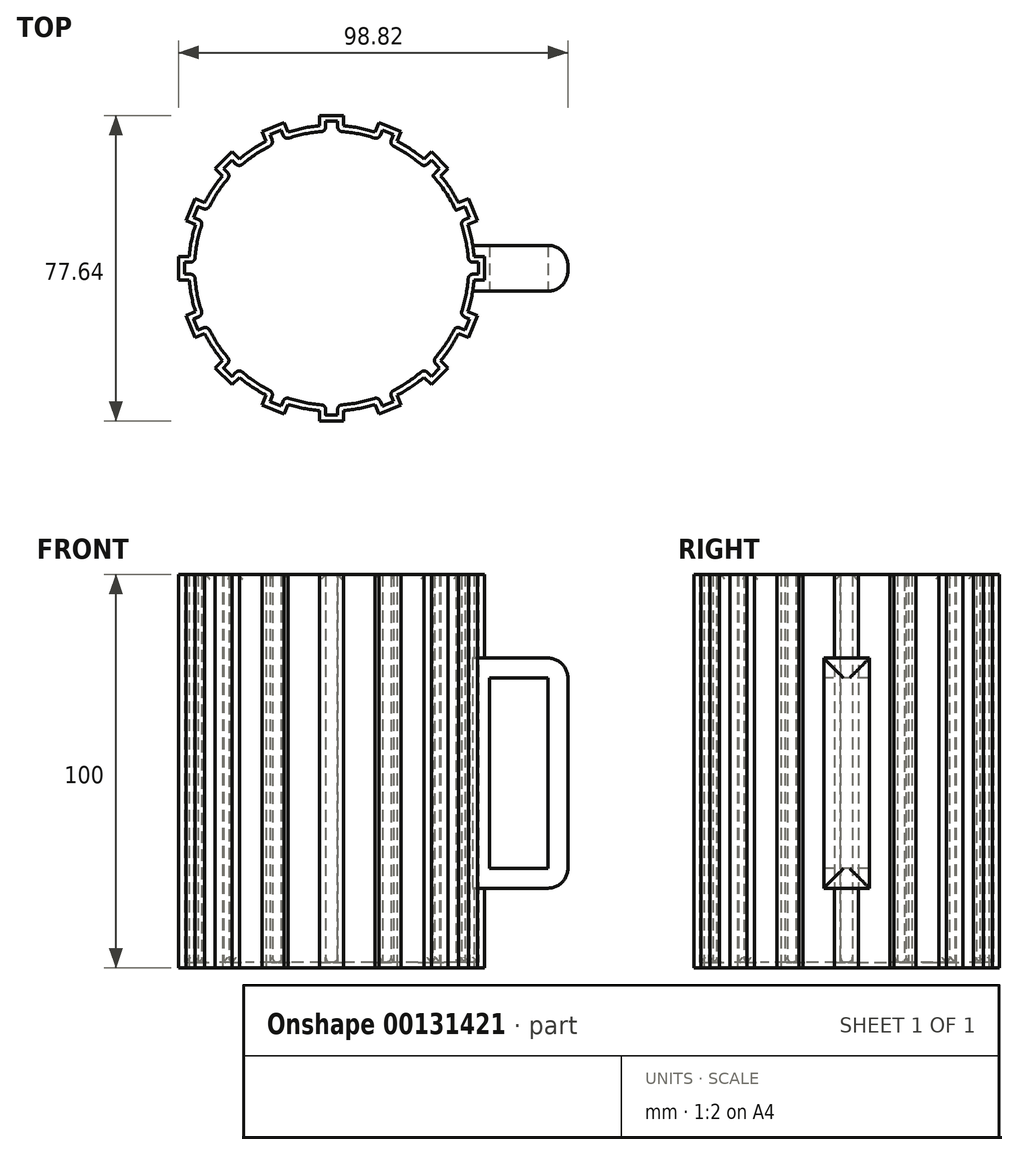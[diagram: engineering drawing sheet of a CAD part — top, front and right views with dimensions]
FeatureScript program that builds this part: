
annotation { "Feature Type Name" : "Feature", "Feature Type Description" : "" }
export const myFeature = defineFeature(function(context is Context, id is Id, definition is map)
    precondition{}
    {
        {
            var Q0;
            Q0=qCreatedBy(makeId("Top.planeOp"),FACE);
            var sketch = newSketch(context, id + "F0", { "sketchPlane" : qUnion([Q0])});
            skCircle(sketch, "E0", {"center": v(0, 0) * mm, "radius": 36.3 * mm});
            skLineSegment(sketch, "E1.bottom", {"start": v(3.02, 38.82) * mm, "end": v(-3.02, 38.82) * mm});
            skLineSegment(sketch, "E1.top", {"start": v(3.02, 33.79) * mm, "end": v(-3.02, 33.79) * mm});
            skLineSegment(sketch, "E1.left", {"start": v(3.02, 38.82) * mm, "end": v(3.02, 33.79) * mm});
            skLineSegment(sketch, "E1.right", {"start": v(-3.02, 38.82) * mm, "end": v(-3.02, 33.79) * mm});
            skPoint(sketch, "E1.middle", {"position": v(0, 36.3) * mm});
            skLineSegment(sketch, "E2.1.0", {"start": v(12.07, 37.02) * mm, "end": v(10.14, 32.37) * mm});
            skLineSegment(sketch, "E2.1.1", {"start": v(17.65, 34.7) * mm, "end": v(12.07, 37.02) * mm});
            skLineSegment(sketch, "E2.1.2", {"start": v(17.65, 34.7) * mm, "end": v(15.72, 30.06) * mm});
            skLineSegment(sketch, "E2.2.0", {"start": v(25.32, 29.59) * mm, "end": v(21.76, 26.03) * mm});
            skLineSegment(sketch, "E2.2.1", {"start": v(29.59, 25.32) * mm, "end": v(25.32, 29.59) * mm});
            skLineSegment(sketch, "E2.2.2", {"start": v(29.59, 25.32) * mm, "end": v(26.03, 21.76) * mm});
            skLineSegment(sketch, "E2.3.0", {"start": v(34.7, 17.65) * mm, "end": v(30.06, 15.72) * mm});
            skLineSegment(sketch, "E2.3.1", {"start": v(37.02, 12.07) * mm, "end": v(34.7, 17.65) * mm});
            skLineSegment(sketch, "E2.3.2", {"start": v(37.02, 12.07) * mm, "end": v(32.37, 10.14) * mm});
            skLineSegment(sketch, "E2.4.0", {"start": v(38.82, 3.02) * mm, "end": v(33.79, 3.02) * mm});
            skLineSegment(sketch, "E2.4.1", {"start": v(38.82, -3.02) * mm, "end": v(38.82, 3.02) * mm});
            skLineSegment(sketch, "E2.4.2", {"start": v(38.82, -3.02) * mm, "end": v(33.79, -3.02) * mm});
            skLineSegment(sketch, "E2.5.0", {"start": v(37.02, -12.07) * mm, "end": v(32.37, -10.14) * mm});
            skLineSegment(sketch, "E2.5.1", {"start": v(34.7, -17.65) * mm, "end": v(37.02, -12.07) * mm});
            skLineSegment(sketch, "E2.5.2", {"start": v(34.7, -17.65) * mm, "end": v(30.06, -15.72) * mm});
            skLineSegment(sketch, "E2.6.0", {"start": v(29.59, -25.32) * mm, "end": v(26.03, -21.76) * mm});
            skLineSegment(sketch, "E2.6.1", {"start": v(25.32, -29.59) * mm, "end": v(29.59, -25.32) * mm});
            skLineSegment(sketch, "E2.6.2", {"start": v(25.32, -29.59) * mm, "end": v(21.76, -26.03) * mm});
            skLineSegment(sketch, "E2.7.0", {"start": v(17.65, -34.7) * mm, "end": v(15.72, -30.06) * mm});
            skLineSegment(sketch, "E2.7.1", {"start": v(12.07, -37.02) * mm, "end": v(17.65, -34.7) * mm});
            skLineSegment(sketch, "E2.7.2", {"start": v(12.07, -37.02) * mm, "end": v(10.14, -32.37) * mm});
            skLineSegment(sketch, "E2.8.0", {"start": v(3.02, -38.82) * mm, "end": v(3.02, -33.79) * mm});
            skLineSegment(sketch, "E2.8.1", {"start": v(-3.02, -38.82) * mm, "end": v(3.02, -38.82) * mm});
            skLineSegment(sketch, "E2.8.2", {"start": v(-3.02, -38.82) * mm, "end": v(-3.02, -33.79) * mm});
            skLineSegment(sketch, "E2.9.0", {"start": v(-12.07, -37.02) * mm, "end": v(-10.14, -32.37) * mm});
            skLineSegment(sketch, "E2.9.1", {"start": v(-17.65, -34.7) * mm, "end": v(-12.07, -37.02) * mm});
            skLineSegment(sketch, "E2.9.2", {"start": v(-17.65, -34.7) * mm, "end": v(-15.72, -30.06) * mm});
            skLineSegment(sketch, "E2.10.0", {"start": v(-25.32, -29.59) * mm, "end": v(-21.76, -26.03) * mm});
            skLineSegment(sketch, "E2.10.1", {"start": v(-29.59, -25.32) * mm, "end": v(-25.32, -29.59) * mm});
            skLineSegment(sketch, "E2.10.2", {"start": v(-29.59, -25.32) * mm, "end": v(-26.03, -21.76) * mm});
            skLineSegment(sketch, "E2.11.0", {"start": v(-34.7, -17.65) * mm, "end": v(-30.06, -15.72) * mm});
            skLineSegment(sketch, "E2.11.1", {"start": v(-37.02, -12.07) * mm, "end": v(-34.7, -17.65) * mm});
            skLineSegment(sketch, "E2.11.2", {"start": v(-37.02, -12.07) * mm, "end": v(-32.37, -10.14) * mm});
            skLineSegment(sketch, "E2.12.0", {"start": v(-38.82, -3.02) * mm, "end": v(-33.79, -3.02) * mm});
            skLineSegment(sketch, "E2.12.1", {"start": v(-38.82, 3.02) * mm, "end": v(-38.82, -3.02) * mm});
            skLineSegment(sketch, "E2.12.2", {"start": v(-38.82, 3.02) * mm, "end": v(-33.79, 3.02) * mm});
            skLineSegment(sketch, "E2.13.0", {"start": v(-37.02, 12.07) * mm, "end": v(-32.37, 10.14) * mm});
            skLineSegment(sketch, "E2.13.1", {"start": v(-34.7, 17.65) * mm, "end": v(-37.02, 12.07) * mm});
            skLineSegment(sketch, "E2.13.2", {"start": v(-34.7, 17.65) * mm, "end": v(-30.06, 15.72) * mm});
            skLineSegment(sketch, "E2.14.0", {"start": v(-29.59, 25.32) * mm, "end": v(-26.03, 21.76) * mm});
            skLineSegment(sketch, "E2.14.1", {"start": v(-25.32, 29.59) * mm, "end": v(-29.59, 25.32) * mm});
            skLineSegment(sketch, "E2.14.2", {"start": v(-25.32, 29.59) * mm, "end": v(-21.76, 26.03) * mm});
            skLineSegment(sketch, "E2.15.0", {"start": v(-17.65, 34.7) * mm, "end": v(-15.72, 30.06) * mm});
            skLineSegment(sketch, "E2.15.1", {"start": v(-12.07, 37.02) * mm, "end": v(-17.65, 34.7) * mm});
            skLineSegment(sketch, "E2.15.2", {"start": v(-12.07, 37.02) * mm, "end": v(-10.14, 32.37) * mm});
            skLineSegment(sketch, "E2.anchor1", {"start": v(0, 0) * mm, "end": v(-3.02, 33.79) * mm, "construction": true});
            skLineSegment(sketch, "E2.anchor2", {"start": v(0, 0) * mm, "end": v(-15.72, 30.06) * mm, "construction": true});
            skSolve(sketch);
        }
        {
            var Q0;
            Q0 = qSketchRegion(id + "F0", true);
            extrude(context, id + "F1", {"entities" : qUnion([Q0]), "depth" : 100 * mm});
        }
        {
            var Q0;
            Q0=makeQuery(id+"F1.opExtrude","CAP_FACE",FACE,{"disambiguationData":[OSD([sQuery(id+"F0.wireOp",EDGE,"E0"),sQuery(id+"F0.wireOp",EDGE,"E1.bottom"),sQuery(id+"F0.wireOp",EDGE,"E1.left"),sQuery(id+"F0.wireOp",EDGE,"E1.right"),sQuery(id+"F0.wireOp",EDGE,"E2.1.0"),sQuery(id+"F0.wireOp",EDGE,"E2.1.1"),sQuery(id+"F0.wireOp",EDGE,"E2.1.2"),sQuery(id+"F0.wireOp",EDGE,"E2.2.0"),sQuery(id+"F0.wireOp",EDGE,"E2.2.1"),sQuery(id+"F0.wireOp",EDGE,"E2.2.2"),sQuery(id+"F0.wireOp",EDGE,"E2.3.0"),sQuery(id+"F0.wireOp",EDGE,"E2.3.1"),sQuery(id+"F0.wireOp",EDGE,"E2.3.2"),sQuery(id+"F0.wireOp",EDGE,"E2.4.0"),sQuery(id+"F0.wireOp",EDGE,"E2.4.1"),sQuery(id+"F0.wireOp",EDGE,"E2.4.2"),sQuery(id+"F0.wireOp",EDGE,"E2.5.0"),sQuery(id+"F0.wireOp",EDGE,"E2.5.1"),sQuery(id+"F0.wireOp",EDGE,"E2.5.2"),sQuery(id+"F0.wireOp",EDGE,"E2.6.0"),sQuery(id+"F0.wireOp",EDGE,"E2.6.1"),sQuery(id+"F0.wireOp",EDGE,"E2.6.2"),sQuery(id+"F0.wireOp",EDGE,"E2.7.0"),sQuery(id+"F0.wireOp",EDGE,"E2.7.1"),sQuery(id+"F0.wireOp",EDGE,"E2.7.2"),sQuery(id+"F0.wireOp",EDGE,"E2.8.0"),sQuery(id+"F0.wireOp",EDGE,"E2.8.1"),sQuery(id+"F0.wireOp",EDGE,"E2.8.2"),sQuery(id+"F0.wireOp",EDGE,"E2.9.0"),sQuery(id+"F0.wireOp",EDGE,"E2.9.1"),sQuery(id+"F0.wireOp",EDGE,"E2.9.2"),sQuery(id+"F0.wireOp",EDGE,"E2.10.0"),sQuery(id+"F0.wireOp",EDGE,"E2.10.1"),sQuery(id+"F0.wireOp",EDGE,"E2.10.2"),sQuery(id+"F0.wireOp",EDGE,"E2.11.0"),sQuery(id+"F0.wireOp",EDGE,"E2.11.1"),sQuery(id+"F0.wireOp",EDGE,"E2.11.2"),sQuery(id+"F0.wireOp",EDGE,"E2.12.0"),sQuery(id+"F0.wireOp",EDGE,"E2.12.1"),sQuery(id+"F0.wireOp",EDGE,"E2.12.2"),sQuery(id+"F0.wireOp",EDGE,"E2.13.0"),sQuery(id+"F0.wireOp",EDGE,"E2.13.1"),sQuery(id+"F0.wireOp",EDGE,"E2.13.2"),sQuery(id+"F0.wireOp",EDGE,"E2.14.0"),sQuery(id+"F0.wireOp",EDGE,"E2.14.1"),sQuery(id+"F0.wireOp",EDGE,"E2.14.2"),sQuery(id+"F0.wireOp",EDGE,"E2.15.0"),sQuery(id+"F0.wireOp",EDGE,"E2.15.1"),sQuery(id+"F0.wireOp",EDGE,"E2.15.2")])],"isStart":false});
            shell(context, id + "F2", {"entities" : qUnion([Q0]), "thickness" : 1.5 * mm});
        }
        {
            var Q0;
            Q0=makeQuery(id+"F2.opShell","OFFSET_FACE",FACE,{"disambiguationData":[OSD([sQuery(id+"F0.wireOp",EDGE,"E0"),sQuery(id+"F0.wireOp",EDGE,"E1.bottom"),sQuery(id+"F0.wireOp",EDGE,"E1.left"),sQuery(id+"F0.wireOp",EDGE,"E1.right"),sQuery(id+"F0.wireOp",EDGE,"E2.1.0"),sQuery(id+"F0.wireOp",EDGE,"E2.1.1"),sQuery(id+"F0.wireOp",EDGE,"E2.1.2"),sQuery(id+"F0.wireOp",EDGE,"E2.2.0"),sQuery(id+"F0.wireOp",EDGE,"E2.2.1"),sQuery(id+"F0.wireOp",EDGE,"E2.2.2"),sQuery(id+"F0.wireOp",EDGE,"E2.3.0"),sQuery(id+"F0.wireOp",EDGE,"E2.3.1"),sQuery(id+"F0.wireOp",EDGE,"E2.3.2"),sQuery(id+"F0.wireOp",EDGE,"E2.4.0"),sQuery(id+"F0.wireOp",EDGE,"E2.4.1"),sQuery(id+"F0.wireOp",EDGE,"E2.4.2"),sQuery(id+"F0.wireOp",EDGE,"E2.5.0"),sQuery(id+"F0.wireOp",EDGE,"E2.5.1"),sQuery(id+"F0.wireOp",EDGE,"E2.5.2"),sQuery(id+"F0.wireOp",EDGE,"E2.6.0"),sQuery(id+"F0.wireOp",EDGE,"E2.6.1"),sQuery(id+"F0.wireOp",EDGE,"E2.6.2"),sQuery(id+"F0.wireOp",EDGE,"E2.7.0"),sQuery(id+"F0.wireOp",EDGE,"E2.7.1"),sQuery(id+"F0.wireOp",EDGE,"E2.7.2"),sQuery(id+"F0.wireOp",EDGE,"E2.8.0"),sQuery(id+"F0.wireOp",EDGE,"E2.8.1"),sQuery(id+"F0.wireOp",EDGE,"E2.8.2"),sQuery(id+"F0.wireOp",EDGE,"E2.9.0"),sQuery(id+"F0.wireOp",EDGE,"E2.9.1"),sQuery(id+"F0.wireOp",EDGE,"E2.9.2"),sQuery(id+"F0.wireOp",EDGE,"E2.10.0"),sQuery(id+"F0.wireOp",EDGE,"E2.10.1"),sQuery(id+"F0.wireOp",EDGE,"E2.10.2"),sQuery(id+"F0.wireOp",EDGE,"E2.11.0"),sQuery(id+"F0.wireOp",EDGE,"E2.11.1"),sQuery(id+"F0.wireOp",EDGE,"E2.11.2"),sQuery(id+"F0.wireOp",EDGE,"E2.12.0"),sQuery(id+"F0.wireOp",EDGE,"E2.12.1"),sQuery(id+"F0.wireOp",EDGE,"E2.12.2"),sQuery(id+"F0.wireOp",EDGE,"E2.13.0"),sQuery(id+"F0.wireOp",EDGE,"E2.13.1"),sQuery(id+"F0.wireOp",EDGE,"E2.13.2"),sQuery(id+"F0.wireOp",EDGE,"E2.14.0"),sQuery(id+"F0.wireOp",EDGE,"E2.14.1"),sQuery(id+"F0.wireOp",EDGE,"E2.14.2"),sQuery(id+"F0.wireOp",EDGE,"E2.15.0"),sQuery(id+"F0.wireOp",EDGE,"E2.15.1"),sQuery(id+"F0.wireOp",EDGE,"E2.15.2")])]});
            extrude(context, id + "F3", {"entities" : qUnion([Q0]), "operationType" : NewBodyOperationType.REMOVE, "depth" : 25 * mm});
        }
        {
            var Q0;
            Q0=qCreatedBy(makeId("Right.planeOp"),FACE);
            cPlane(context, id + "F4", {"entities" : qUnion([Q0]), "cplaneType" : CPlaneType.OFFSET, "offset" : 60 * mm, "width" : 150 * mm, "height" : 150 * mm});
        }
        {
            var Q0;
            Q0=qCreatedBy(id+"F4.planeOp",FACE);
            var sketch = newSketch(context, id + "F5", { "sketchPlane" : qUnion([Q0])});
            skLineSegment(sketch, "E3.bottom", {"start": v(-5.81, 20.3) * mm, "end": v(5.81, 20.3) * mm});
            skLineSegment(sketch, "E3.top", {"start": v(-5.81, 78.76) * mm, "end": v(5.81, 78.76) * mm});
            skLineSegment(sketch, "E3.left", {"start": v(-5.81, 20.3) * mm, "end": v(-5.81, 78.76) * mm});
            skLineSegment(sketch, "E3.right", {"start": v(5.81, 20.3) * mm, "end": v(5.81, 78.76) * mm});
            skPoint(sketch, "E3.middle", {"position": v(0, 49.53) * mm});
            skSolve(sketch);
        }
        {
            var Q0;
            Q0 = qSketchRegion(id + "F5", true);
            var Q1;
            Q1=makeQuery(id+"F1.opExtrude","SWEPT_BODY",BODY,{"disambiguationData":[OSD([sQuery(id+"F0.wireOp",EDGE,"E0"),sQuery(id+"F0.wireOp",EDGE,"E1.bottom"),sQuery(id+"F0.wireOp",EDGE,"E1.left"),sQuery(id+"F0.wireOp",EDGE,"E1.right"),sQuery(id+"F0.wireOp",EDGE,"E2.1.0"),sQuery(id+"F0.wireOp",EDGE,"E2.1.1"),sQuery(id+"F0.wireOp",EDGE,"E2.1.2"),sQuery(id+"F0.wireOp",EDGE,"E2.2.0"),sQuery(id+"F0.wireOp",EDGE,"E2.2.1"),sQuery(id+"F0.wireOp",EDGE,"E2.2.2"),sQuery(id+"F0.wireOp",EDGE,"E2.3.0"),sQuery(id+"F0.wireOp",EDGE,"E2.3.1"),sQuery(id+"F0.wireOp",EDGE,"E2.3.2"),sQuery(id+"F0.wireOp",EDGE,"E2.4.0"),sQuery(id+"F0.wireOp",EDGE,"E2.4.1"),sQuery(id+"F0.wireOp",EDGE,"E2.4.2"),sQuery(id+"F0.wireOp",EDGE,"E2.5.0"),sQuery(id+"F0.wireOp",EDGE,"E2.5.1"),sQuery(id+"F0.wireOp",EDGE,"E2.5.2"),sQuery(id+"F0.wireOp",EDGE,"E2.6.0"),sQuery(id+"F0.wireOp",EDGE,"E2.6.1"),sQuery(id+"F0.wireOp",EDGE,"E2.6.2"),sQuery(id+"F0.wireOp",EDGE,"E2.7.0"),sQuery(id+"F0.wireOp",EDGE,"E2.7.1"),sQuery(id+"F0.wireOp",EDGE,"E2.7.2"),sQuery(id+"F0.wireOp",EDGE,"E2.8.0"),sQuery(id+"F0.wireOp",EDGE,"E2.8.1"),sQuery(id+"F0.wireOp",EDGE,"E2.8.2"),sQuery(id+"F0.wireOp",EDGE,"E2.9.0"),sQuery(id+"F0.wireOp",EDGE,"E2.9.1"),sQuery(id+"F0.wireOp",EDGE,"E2.9.2"),sQuery(id+"F0.wireOp",EDGE,"E2.10.0"),sQuery(id+"F0.wireOp",EDGE,"E2.10.1"),sQuery(id+"F0.wireOp",EDGE,"E2.10.2"),sQuery(id+"F0.wireOp",EDGE,"E2.11.0"),sQuery(id+"F0.wireOp",EDGE,"E2.11.1"),sQuery(id+"F0.wireOp",EDGE,"E2.11.2"),sQuery(id+"F0.wireOp",EDGE,"E2.12.0"),sQuery(id+"F0.wireOp",EDGE,"E2.12.1"),sQuery(id+"F0.wireOp",EDGE,"E2.12.2"),sQuery(id+"F0.wireOp",EDGE,"E2.13.0"),sQuery(id+"F0.wireOp",EDGE,"E2.13.1"),sQuery(id+"F0.wireOp",EDGE,"E2.13.2"),sQuery(id+"F0.wireOp",EDGE,"E2.14.0"),sQuery(id+"F0.wireOp",EDGE,"E2.14.1"),sQuery(id+"F0.wireOp",EDGE,"E2.14.2"),sQuery(id+"F0.wireOp",EDGE,"E2.15.0"),sQuery(id+"F0.wireOp",EDGE,"E2.15.1"),sQuery(id+"F0.wireOp",EDGE,"E2.15.2")])]});
            extrude(context, id + "F6", {"entities" : qUnion([Q0]), "operationType" : NewBodyOperationType.ADD, "endBound" : BoundingType.UP_TO_BODY, "oppositeDirection" : true, "endBoundEntityBody" : qUnion([Q1]), "depth" : 39.13 * mm});
        }
        {
            var Q0;
            Q0=makeQuery(id+"F6.opExtrude","CAP_EDGE",EDGE,{"disambiguationData":[OSD([sQuery(id+"F5.wireOp",EDGE,"E3.top")])],"isStart":true});
            var Q1;
            Q1=makeQuery(id+"F6.opExtrude","CAP_EDGE",EDGE,{"disambiguationData":[OSD([sQuery(id+"F5.wireOp",EDGE,"E3.bottom")])],"isStart":true});
            var Q2;
            Q2=makeQuery(id+"F6.opExtrude","CAP_EDGE",EDGE,{"disambiguationData":[OSD([sQuery(id+"F5.wireOp",EDGE,"E3.left")])],"isStart":true});
            var Q3;
            Q3=makeQuery(id+"F6.opExtrude","CAP_EDGE",EDGE,{"disambiguationData":[OSD([sQuery(id+"F5.wireOp",EDGE,"E3.right")])],"isStart":true});
            fillet(context, id + "F7", {"entities" : qUnion([Q0, Q1, Q2, Q3]), "radius" : 5 * mm, "tangentPropagation" : true, "allowEdgeOverflow" : false});
        }
        {
            var Q0;
            Q0=makeQuery(id+"F6.opExtrude","SWEPT_FACE",FACE,{"disambiguationData":[OSD([sQuery(id+"F5.wireOp",EDGE,"E3.left")])]});
            var sketch = newSketch(context, id + "F8", { "sketchPlane" : qUnion([Q0])});
            skLineSegment(sketch, "E4.bottom", {"start": v(55, 73.76) * mm, "end": v(40.1, 73.76) * mm});
            skLineSegment(sketch, "E4.top", {"start": v(55, 25.3) * mm, "end": v(40.1, 25.3) * mm});
            skLineSegment(sketch, "E4.left", {"start": v(55, 73.76) * mm, "end": v(55, 25.3) * mm});
            skLineSegment(sketch, "E4.right", {"start": v(40.1, 73.76) * mm, "end": v(40.1, 25.3) * mm});
            skSolve(sketch);
        }
        {
            var Q0;
            Q0=makeQuery(id+"F8.imprint","IMPRINT",FACE,{"disambiguationData":[TD([[makeQuery(id+"F8.imprint","IMPRINT",EDGE,{"derivedFrom":sQuery(id+"F8.wireOp",EDGE,"E4.bottom")}),1.0]])]});
            extrude(context, id + "F9", {"entities" : qUnion([Q0]), "operationType" : NewBodyOperationType.REMOVE, "endBound" : BoundingType.THROUGH_ALL, "oppositeDirection" : true, "depth" : 25 * mm});
        }
        {
            var Q0;
            {var subQ0=sQuery(id+"F0.wireOp",EDGE,"E0");Q0=makeQuery(id+"F2.opShell","OFFSET_FACE",FACE,{"disambiguationData":[OSD([subQ0]),TDD([makeQuery(id+"F1.opExtrude","SWEPT_FACE",FACE,{"disambiguationData":[OSD([subQ0]),TDD([makeQuery(id+"F0.imprint","IMPRINT",EDGE,{"disambiguationData":[TD([[makeQuery(id+"F0.imprint","INTERSECT",VERTEX,{"derivedFrom":[subQ0,sQuery(id+"F0.wireOp",EDGE,"E2.15.0")]}),-1.0]])],"derivedFrom":subQ0})])]})])]});}
            var Q1;
            {var subQ0=sQuery(id+"F0.wireOp",EDGE,"E0");Q1=makeQuery(id+"F2.opShell","OFFSET_FACE",FACE,{"disambiguationData":[OSD([subQ0]),TDD([makeQuery(id+"F1.opExtrude","SWEPT_FACE",FACE,{"disambiguationData":[OSD([subQ0]),TDD([makeQuery(id+"F0.imprint","IMPRINT",EDGE,{"disambiguationData":[TD([[makeQuery(id+"F0.imprint","INTERSECT",VERTEX,{"derivedFrom":[subQ0,sQuery(id+"F0.wireOp",EDGE,"E2.15.2")]}),1.0]])],"derivedFrom":subQ0})])]})])]});}
            var Q2;
            {var subQ0=sQuery(id+"F0.wireOp",EDGE,"E0");Q2=makeQuery(id+"F2.opShell","OFFSET_FACE",FACE,{"disambiguationData":[OSD([subQ0]),TDD([makeQuery(id+"F1.opExtrude","SWEPT_FACE",FACE,{"disambiguationData":[OSD([subQ0]),TDD([makeQuery(id+"F0.imprint","IMPRINT",EDGE,{"disambiguationData":[TD([[makeQuery(id+"F0.imprint","INTERSECT",VERTEX,{"derivedFrom":[subQ0,sQuery(id+"F0.wireOp",EDGE,"E2.1.0")]}),-1.0]])],"derivedFrom":subQ0})])]})])]});}
            var Q3;
            Q3=makeQuery(id+"F2.opShell","OFFSET_EDGE",EDGE,{"disambiguationData":[OSD([sQuery(id+"F0.wireOp",EDGE,"E0"),sQuery(id+"F0.wireOp",EDGE,"E2.2.0")])]});
            var Q4;
            {var subQ0=sQuery(id+"F0.wireOp",EDGE,"E0");Q4=makeQuery(id+"F2.opShell","OFFSET_FACE",FACE,{"disambiguationData":[OSD([subQ0]),TDD([makeQuery(id+"F1.opExtrude","SWEPT_FACE",FACE,{"disambiguationData":[OSD([subQ0]),TDD([makeQuery(id+"F0.imprint","IMPRINT",EDGE,{"disambiguationData":[TD([[makeQuery(id+"F0.imprint","INTERSECT",VERTEX,{"derivedFrom":[subQ0,sQuery(id+"F0.wireOp",EDGE,"E2.2.0")]}),-1.0]])],"derivedFrom":subQ0})])]})])]});}
            var Q5;
            {var subQ0=sQuery(id+"F0.wireOp",EDGE,"E0");Q5=makeQuery(id+"F2.opShell","OFFSET_FACE",FACE,{"disambiguationData":[OSD([subQ0]),TDD([makeQuery(id+"F1.opExtrude","SWEPT_FACE",FACE,{"disambiguationData":[OSD([subQ0]),TDD([makeQuery(id+"F0.imprint","IMPRINT",EDGE,{"disambiguationData":[TD([[makeQuery(id+"F0.imprint","INTERSECT",VERTEX,{"derivedFrom":[subQ0,sQuery(id+"F0.wireOp",EDGE,"E2.14.0")]}),-1.0]])],"derivedFrom":subQ0})])]})])]});}
            var Q6;
            {var subQ0=sQuery(id+"F0.wireOp",EDGE,"E0");Q6=makeQuery(id+"F2.opShell","OFFSET_FACE",FACE,{"disambiguationData":[OSD([subQ0]),TDD([makeQuery(id+"F1.opExtrude","SWEPT_FACE",FACE,{"disambiguationData":[OSD([subQ0]),TDD([makeQuery(id+"F0.imprint","IMPRINT",EDGE,{"disambiguationData":[TD([[makeQuery(id+"F0.imprint","INTERSECT",VERTEX,{"derivedFrom":[subQ0,sQuery(id+"F0.wireOp",EDGE,"E2.13.0")]}),-1.0]])],"derivedFrom":subQ0})])]})])]});}
            var Q7;
            {var subQ0=sQuery(id+"F0.wireOp",EDGE,"E0");Q7=makeQuery(id+"F2.opShell","OFFSET_FACE",FACE,{"disambiguationData":[OSD([subQ0]),TDD([makeQuery(id+"F1.opExtrude","SWEPT_FACE",FACE,{"disambiguationData":[OSD([subQ0]),TDD([makeQuery(id+"F0.imprint","IMPRINT",EDGE,{"disambiguationData":[TD([[makeQuery(id+"F0.imprint","INTERSECT",VERTEX,{"derivedFrom":[subQ0,sQuery(id+"F0.wireOp",EDGE,"E2.12.0")]}),-1.0]])],"derivedFrom":subQ0})])]})])]});}
            var Q8;
            {var subQ0=sQuery(id+"F0.wireOp",EDGE,"E0");Q8=makeQuery(id+"F2.opShell","OFFSET_FACE",FACE,{"disambiguationData":[OSD([subQ0]),TDD([makeQuery(id+"F1.opExtrude","SWEPT_FACE",FACE,{"disambiguationData":[OSD([subQ0]),TDD([makeQuery(id+"F0.imprint","IMPRINT",EDGE,{"disambiguationData":[TD([[makeQuery(id+"F0.imprint","INTERSECT",VERTEX,{"derivedFrom":[subQ0,sQuery(id+"F0.wireOp",EDGE,"E2.11.0")]}),-1.0]])],"derivedFrom":subQ0})])]})])]});}
            var Q9;
            {var subQ0=sQuery(id+"F0.wireOp",EDGE,"E0");Q9=makeQuery(id+"F2.opShell","OFFSET_FACE",FACE,{"disambiguationData":[OSD([subQ0]),TDD([makeQuery(id+"F1.opExtrude","SWEPT_FACE",FACE,{"disambiguationData":[OSD([subQ0]),TDD([makeQuery(id+"F0.imprint","IMPRINT",EDGE,{"disambiguationData":[TD([[makeQuery(id+"F0.imprint","INTERSECT",VERTEX,{"derivedFrom":[subQ0,sQuery(id+"F0.wireOp",EDGE,"E2.10.0")]}),-1.0]])],"derivedFrom":subQ0})])]})])]});}
            var Q10;
            {var subQ0=sQuery(id+"F0.wireOp",EDGE,"E0");Q10=makeQuery(id+"F2.opShell","OFFSET_FACE",FACE,{"disambiguationData":[OSD([subQ0]),TDD([makeQuery(id+"F1.opExtrude","SWEPT_FACE",FACE,{"disambiguationData":[OSD([subQ0]),TDD([makeQuery(id+"F0.imprint","IMPRINT",EDGE,{"disambiguationData":[TD([[makeQuery(id+"F0.imprint","INTERSECT",VERTEX,{"derivedFrom":[subQ0,sQuery(id+"F0.wireOp",EDGE,"E2.9.0")]}),-1.0]])],"derivedFrom":subQ0})])]})])]});}
            var Q11;
            {var subQ0=sQuery(id+"F0.wireOp",EDGE,"E0");Q11=makeQuery(id+"F2.opShell","OFFSET_FACE",FACE,{"disambiguationData":[OSD([subQ0]),TDD([makeQuery(id+"F1.opExtrude","SWEPT_FACE",FACE,{"disambiguationData":[OSD([subQ0]),TDD([makeQuery(id+"F0.imprint","IMPRINT",EDGE,{"disambiguationData":[TD([[makeQuery(id+"F0.imprint","INTERSECT",VERTEX,{"derivedFrom":[subQ0,sQuery(id+"F0.wireOp",EDGE,"E2.8.0")]}),-1.0]])],"derivedFrom":subQ0})])]})])]});}
            var Q12;
            {var subQ0=sQuery(id+"F0.wireOp",EDGE,"E0");Q12=makeQuery(id+"F2.opShell","OFFSET_FACE",FACE,{"disambiguationData":[OSD([subQ0]),TDD([makeQuery(id+"F1.opExtrude","SWEPT_FACE",FACE,{"disambiguationData":[OSD([subQ0]),TDD([makeQuery(id+"F0.imprint","IMPRINT",EDGE,{"disambiguationData":[TD([[makeQuery(id+"F0.imprint","INTERSECT",VERTEX,{"derivedFrom":[subQ0,sQuery(id+"F0.wireOp",EDGE,"E2.7.0")]}),-1.0]])],"derivedFrom":subQ0})])]})])]});}
            var Q13;
            {var subQ0=sQuery(id+"F0.wireOp",EDGE,"E0");Q13=makeQuery(id+"F2.opShell","OFFSET_FACE",FACE,{"disambiguationData":[OSD([subQ0]),TDD([makeQuery(id+"F1.opExtrude","SWEPT_FACE",FACE,{"disambiguationData":[OSD([subQ0]),TDD([makeQuery(id+"F0.imprint","IMPRINT",EDGE,{"disambiguationData":[TD([[makeQuery(id+"F0.imprint","INTERSECT",VERTEX,{"derivedFrom":[subQ0,sQuery(id+"F0.wireOp",EDGE,"E2.6.0")]}),-1.0]])],"derivedFrom":subQ0})])]})])]});}
            var Q14;
            {var subQ0=sQuery(id+"F0.wireOp",EDGE,"E0");Q14=makeQuery(id+"F2.opShell","OFFSET_FACE",FACE,{"disambiguationData":[OSD([subQ0]),TDD([makeQuery(id+"F1.opExtrude","SWEPT_FACE",FACE,{"disambiguationData":[OSD([subQ0]),TDD([makeQuery(id+"F0.imprint","IMPRINT",EDGE,{"disambiguationData":[TD([[makeQuery(id+"F0.imprint","INTERSECT",VERTEX,{"derivedFrom":[subQ0,sQuery(id+"F0.wireOp",EDGE,"E2.5.0")]}),-1.0]])],"derivedFrom":subQ0})])]})])]});}
            var Q15;
            {var subQ0=sQuery(id+"F0.wireOp",EDGE,"E0");Q15=makeQuery(id+"F2.opShell","OFFSET_EDGE",EDGE,{"disambiguationData":[OSD([subQ0]),TDD([makeQuery(id+"F1.opExtrude","CAP_EDGE",EDGE,{"disambiguationData":[OSD([subQ0]),TDD([makeQuery(id+"F0.imprint","IMPRINT",EDGE,{"disambiguationData":[TD([[makeQuery(id+"F0.imprint","INTERSECT",VERTEX,{"derivedFrom":[subQ0,sQuery(id+"F0.wireOp",EDGE,"E2.3.0")]}),-1.0]])],"derivedFrom":subQ0})])],"isStart":false})])]});}
            var Q16;
            {var subQ0=sQuery(id+"F0.wireOp",EDGE,"E0");Q16=makeQuery(id+"F2.opShell","OFFSET_FACE",FACE,{"disambiguationData":[OSD([subQ0]),TDD([makeQuery(id+"F1.opExtrude","SWEPT_FACE",FACE,{"disambiguationData":[OSD([subQ0]),TDD([makeQuery(id+"F0.imprint","IMPRINT",EDGE,{"disambiguationData":[TD([[makeQuery(id+"F0.imprint","INTERSECT",VERTEX,{"derivedFrom":[subQ0,sQuery(id+"F0.wireOp",EDGE,"E2.3.2")]}),1.0]])],"derivedFrom":subQ0})])]})])]});}
            fillet(context, id + "F10", {"entities" : qUnion([Q0, Q1, Q2, Q3, Q4, Q5, Q6, Q7, Q8, Q9, Q10, Q11, Q12, Q13, Q14, Q15, Q16]), "radius" : 1.2 * mm, "tangentPropagation" : true, "allowEdgeOverflow" : false});
        }
    });
